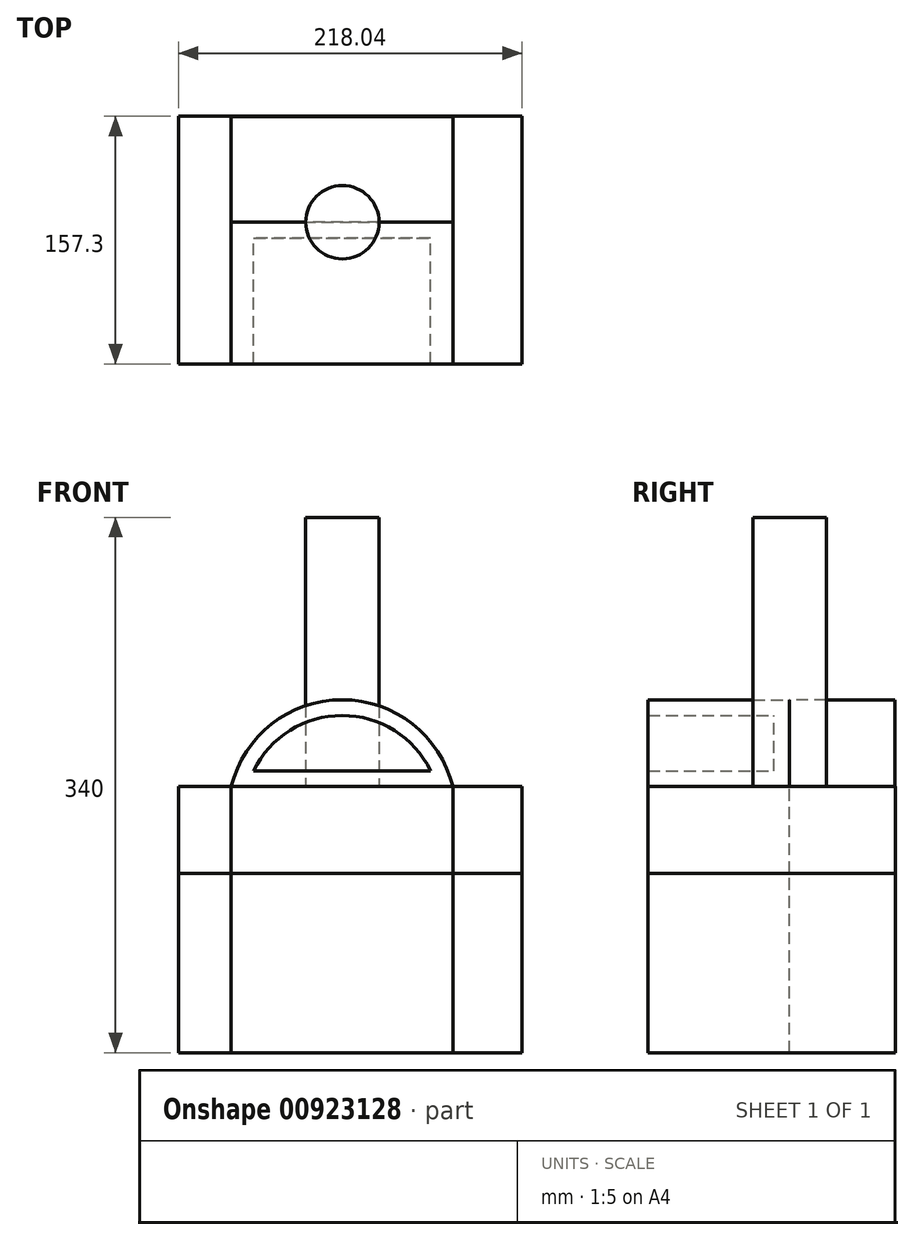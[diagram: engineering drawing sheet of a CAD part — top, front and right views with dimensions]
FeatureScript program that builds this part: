
annotation { "Feature Type Name" : "Feature", "Feature Type Description" : "" }
export const myFeature = defineFeature(function(context is Context, id is Id, definition is map)
    precondition{}
    {
        {
            var Q0;
            Q0=qCreatedBy(makeId("Front.planeOp"),FACE);
            var sketch = newSketch(context, id + "F0", { "sketchPlane" : qUnion([Q0])});
            skArc(sketch, "E0", {"start": v(70.18, 0) * mm, "mid": v(-0.24, 55.18) * mm, "end": v(-70.67, 0) * mm});
            skLineSegment(sketch, "E1", {"start": v(-70.67, 0) * mm, "end": v(70.18, 0) * mm});
            skSolve(sketch);
        }
        {
            var Q0;
            Q0=makeQuery(id+"F0.imprint","IMPRINT",FACE,{"disambiguationData":[TD([[makeQuery(id+"F0.imprint","IMPRINT",EDGE,{"derivedFrom":sQuery(id+"F0.wireOp",EDGE,"E0")}),1.0]])]});
            extrude(context, id + "F1", {"entities" : qUnion([Q0]), "depth" : 90 * mm, "offsetDistance" : 25 * mm});
        }
        {
            var Q0;
            Q0=makeQuery(id+"F1.opExtrude","CAP_FACE",FACE,{"disambiguationData":[OSD([sQuery(id+"F0.wireOp",EDGE,"E0"),sQuery(id+"F0.wireOp",EDGE,"E1")])],"isStart":false});
            shell(context, id + "F2", {"entities" : qUnion([Q0]), "thickness" : 10 * mm});
        }
        {
            var Q0;
            Q0=makeQuery(id+"F1.opExtrude","SWEPT_FACE",FACE,{"disambiguationData":[OSD([sQuery(id+"F0.wireOp",EDGE,"E1")])]});
            var sketch = newSketch(context, id + "F3", { "sketchPlane" : qUnion([Q0])});
            skLineSegment(sketch, "E2.bottom", {"start": v(-104.04, 90) * mm, "end": v(89, 90) * mm});
            skLineSegment(sketch, "E2.top", {"start": v(-104.04, -67.3) * mm, "end": v(89, -67.3) * mm});
            skLineSegment(sketch, "E2.left", {"start": v(-104.04, 90) * mm, "end": v(-104.04, -67.3) * mm});
            skLineSegment(sketch, "E2.right", {"start": v(89, 90) * mm, "end": v(89, -67.3) * mm});
            skSolve(sketch);
        }
        {
            var Q0;
            Q0=makeQuery(id+"F3.imprint","IMPRINT",FACE,{"disambiguationData":[TD([[makeQuery(id+"F3.imprint","IMPRINT",EDGE,{"derivedFrom":sQuery(id+"F3.wireOp",EDGE,"E2.top")}),1.0]])]});
            extrude(context, id + "F4", {"entities" : qUnion([Q0]), "depth" : 55 * mm, "offsetDistance" : 25 * mm});
        }
        {
            var Q0;
            Q0=makeQuery(id+"F1.opExtrude","SWEPT_FACE",FACE,{"disambiguationData":[OSD([sQuery(id+"F0.wireOp",EDGE,"E1")])]});
            extrude(context, id + "F5", {"entities" : qUnion([Q0]), "depth" : 55 * mm, "offsetDistance" : 25 * mm});
        }
        {
            var Q0;
            Q0=makeQuery(id+"F4.opExtrude","SWEPT_FACE",FACE,{"disambiguationData":[OSD([sQuery(id+"F3.wireOp",EDGE,"E2.right")])]});
            extrude(context, id + "F6", {"entities" : qUnion([Q0]), "operationType" : NewBodyOperationType.ADD, "depth" : 25 * mm, "offsetDistance" : 25 * mm});
        }
        {
            var Q0;
            Q0=makeQuery(id+"F1.opExtrude","CAP_FACE",FACE,{"disambiguationData":[OSD([sQuery(id+"F0.wireOp",EDGE,"E0"),sQuery(id+"F0.wireOp",EDGE,"E1")])],"isStart":true});
            extrude(context, id + "F7", {"entities" : qUnion([Q0]), "depth" : 67 * mm, "offsetDistance" : 25 * mm});
        }
        {
            var Q0;
            Q0=makeQuery(id+"F5.opExtrude","CAP_FACE",FACE,{"disambiguationData":[OSD([sQuery(id+"F0.wireOp",EDGE,"E1")])],"isStart":false});
            var Q1;
            {var subQ0=sQuery(id+"F3.wireOp",EDGE,"E2.right");Q1=makeQuery(id+"F6.boolean.opBoolean","MERGE",FACE,{"derivedFrom":[makeQuery(id+"F4.opExtrude","CAP_FACE",FACE,{"disambiguationData":[OSD([sQuery(id+"F0.wireOp",EDGE,"E0"),sQuery(id+"F0.wireOp",EDGE,"E1"),sQuery(id+"F3.wireOp",EDGE,"E2.bottom"),sQuery(id+"F3.wireOp",EDGE,"E2.top"),sQuery(id+"F3.wireOp",EDGE,"E2.left"),subQ0])],"isStart":false}),makeQuery(id+"F6.opExtrude","SWEPT_FACE",FACE,{"disambiguationData":[OSD([subQ0]),TDD([makeQuery(id+"F4.opExtrude","CAP_EDGE",EDGE,{"disambiguationData":[OSD([subQ0])],"isStart":false})])]})]});}
            extrude(context, id + "F8", {"entities" : qUnion([Q0, Q1]), "depth" : 114 * mm, "offsetDistance" : 25 * mm});
        }
        {
            var Q0;
            Q0=qCreatedBy(makeId("Top.planeOp"),FACE);
            var sketch = newSketch(context, id + "F9", { "sketchPlane" : qUnion([Q0])});
            skCircle(sketch, "E3", {"center": v(0, 0) * mm, "radius": 23.28 * mm});
            skSolve(sketch);
        }
        {
            var Q0;
            Q0 = qSketchRegion(id + "F9", true);
            extrude(context, id + "F10", {"entities" : qUnion([Q0]), "depth" : 171 * mm, "offsetDistance" : 25 * mm});
        }
    });
